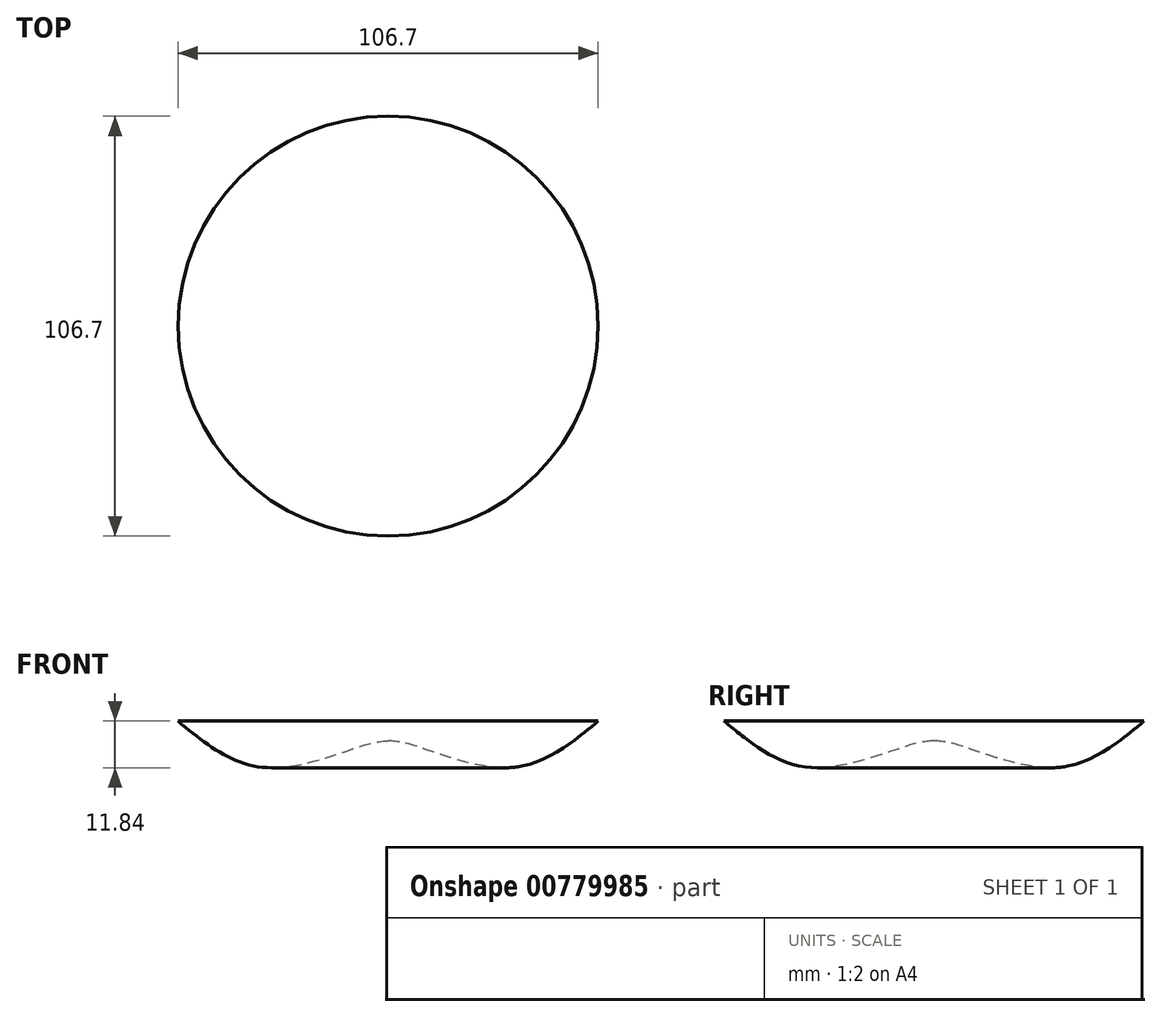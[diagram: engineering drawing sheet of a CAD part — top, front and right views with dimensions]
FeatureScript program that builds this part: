
annotation { "Feature Type Name" : "Feature", "Feature Type Description" : "" }
export const myFeature = defineFeature(function(context is Context, id is Id, definition is map)
    precondition{}
    {
        {
            var Q0;
            Q0=qCreatedBy(makeId("Front.planeOp"),FACE);
            var sketch = newSketch(context, id + "F0", { "sketchPlane" : qUnion([Q0])});
            skLineSegment(sketch, "E0.bottom", {"start": v(0, 0) * mm, "end": v(-53.35, 0) * mm});
            skLineSegment(sketch, "E0.top", {"start": v(0, 22.4) * mm, "end": v(-53.35, 22.4) * mm});
            skLineSegment(sketch, "E0.left", {"start": v(0, 0) * mm, "end": v(0, 22.4) * mm});
            skLineSegment(sketch, "E0.right", {"start": v(-53.35, 0) * mm, "end": v(-53.35, 22.4) * mm});
            skLineSegment(sketch, "E1", {"start": v(0, 0) * mm, "end": v(0, 11.2) * mm});
            skFitSpline(sketch, "E2", {"points": [v(-53.35, 22.4) * mm, v(-30.97, 10.58) * mm, v(-5.4, 16.51) * mm, v(0, 17.36) * mm], "startDerivative": vector(50.63, -42.13) * mm, "endDerivative": vector(22.83, 0.93) * mm});
            skSolve(sketch);
        }
        {
            var Q0;
            {var subQ0=sQuery(id+"F0.wireOp",EDGE,"E0.top");Q0=makeQuery(id+"F0.imprint","IMPRINT",FACE,{"disambiguationData":[TD([[makeQuery(id+"F0.imprint","IMPRINT",EDGE,{"derivedFrom":subQ0}),1.0]])]});}
            var Q1;
            Q1=sQuery(id+"F0.wireOp",EDGE,"E0.left");
            revolve(context, id + "F1", {"surfaceOperationType" : NewSurfaceOperationType.NEW, "entities" : qUnion([Q0]), "axis" : qUnion([Q1]), "revolveType" : RevolveType.FULL});
        }
    });
